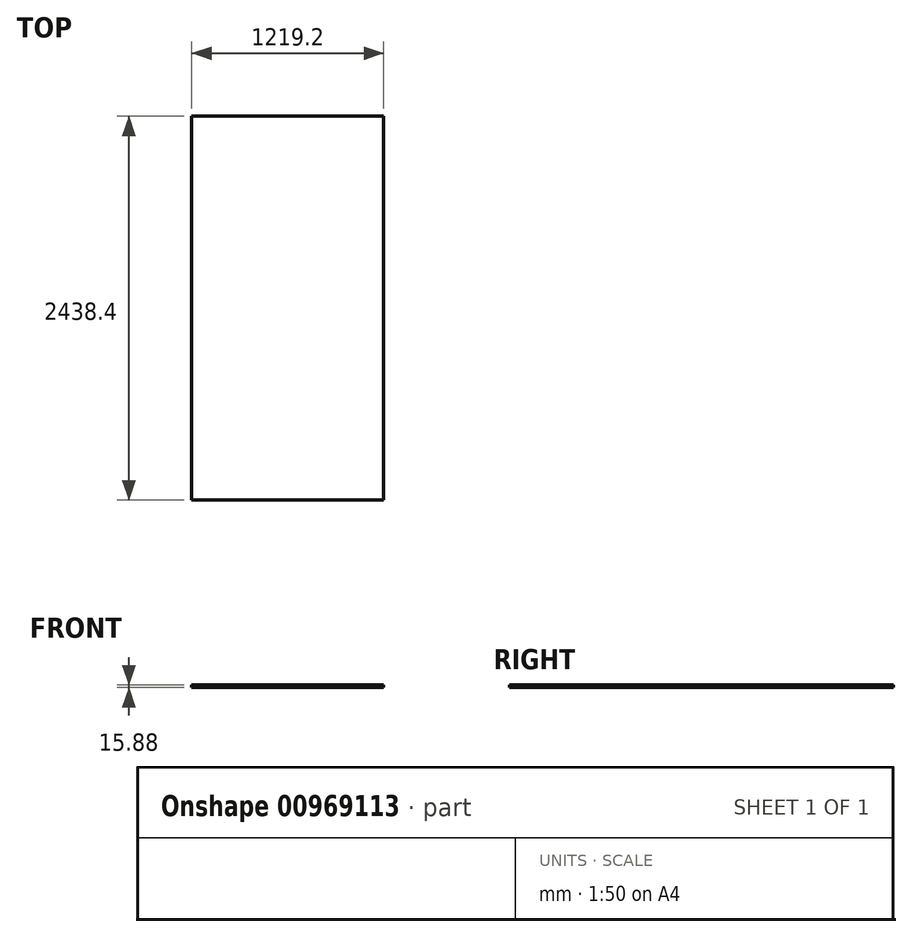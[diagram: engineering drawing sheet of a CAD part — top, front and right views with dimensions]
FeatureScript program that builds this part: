
annotation { "Feature Type Name" : "Feature", "Feature Type Description" : "" }
export const myFeature = defineFeature(function(context is Context, id is Id, definition is map)
    precondition{}
    {
        {
            var Q0;
            Q0=qCreatedBy(makeId("Top.planeOp"),FACE);
            var sketch = newSketch(context, id + "F0", { "sketchPlane" : qUnion([Q0])});
            skLineSegment(sketch, "E0.bottom", {"start": v(0, 0) * mm, "end": v(1219.2, 0) * mm});
            skLineSegment(sketch, "E0.top", {"start": v(0, 2438.4) * mm, "end": v(1219.2, 2438.4) * mm});
            skLineSegment(sketch, "E0.left", {"start": v(0, 0) * mm, "end": v(0, 2438.4) * mm});
            skLineSegment(sketch, "E0.right", {"start": v(1219.2, 0) * mm, "end": v(1219.2, 2438.4) * mm});
            skSolve(sketch);
        }
        {
            var Q0;
            Q0=makeQuery(id+"F0.imprint","IMPRINT",FACE,{"disambiguationData":[TD([[makeQuery(id+"F0.imprint","IMPRINT",EDGE,{"derivedFrom":sQuery(id+"F0.wireOp",EDGE,"E0.bottom")}),1.0]])]});
            extrude(context, id + "F1", {"entities" : qUnion([Q0]), "depth" : 15.88 * mm, "offsetDistance" : 25.4 * mm});
        }
    });
